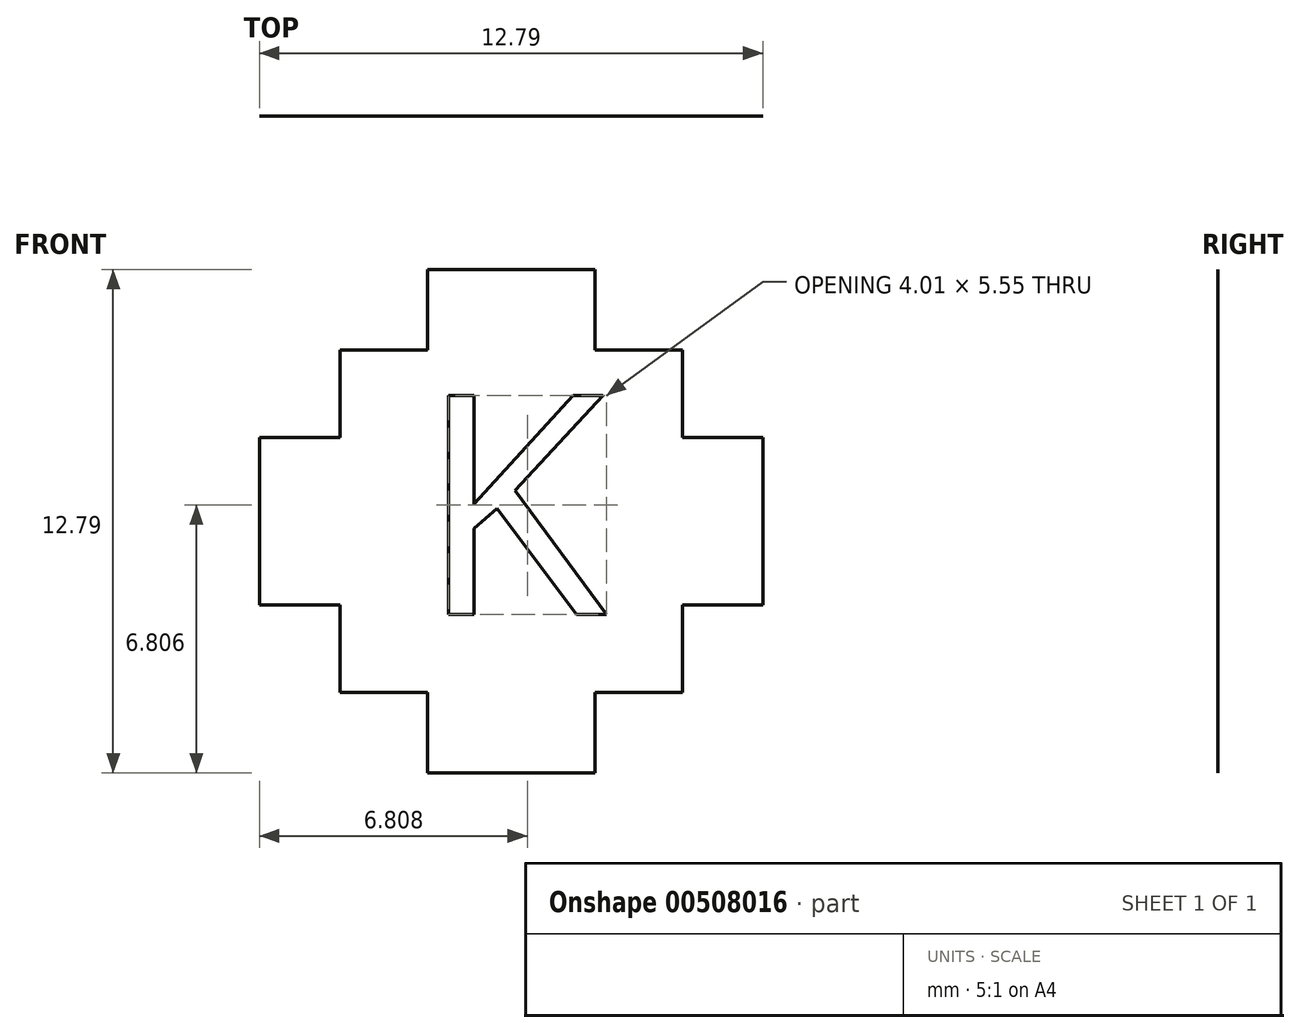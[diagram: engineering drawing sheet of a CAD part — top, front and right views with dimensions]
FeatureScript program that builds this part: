
annotation { "Feature Type Name" : "Feature", "Feature Type Description" : "" }
export const myFeature = defineFeature(function(context is Context, id is Id, definition is map)
    precondition{}
    {
        {
            var Q0;
            Q0=qCreatedBy(makeId("Front.planeOp"),FACE);
            var sketch = newSketch(context, id + "F0", { "sketchPlane" : qUnion([Q0])});
            skLineSegment(sketch, "E0", {"start": v(-17.35, 36.23) * mm, "end": v(-15.22, 36.23) * mm});
            skLineSegment(sketch, "E1", {"start": v(-15.22, 36.23) * mm, "end": v(-15.22, 34.18) * mm});
            skLineSegment(sketch, "E2", {"start": v(-15.22, 34.18) * mm, "end": v(-13, 34.18) * mm});
            skLineSegment(sketch, "E3", {"start": v(-13, 34.18) * mm, "end": v(-13, 31.96) * mm});
            skLineSegment(sketch, "E4", {"start": v(-13, 31.96) * mm, "end": v(-10.95, 31.96) * mm});
            skLineSegment(sketch, "E5", {"start": v(-10.95, 31.96) * mm, "end": v(-10.95, 29.83) * mm});
            skLineSegment(sketch, "E6", {"start": v(-17.35, 36.23) * mm, "end": v(-17.35, 28.94) * mm, "construction": true});
            skLineSegment(sketch, "E7.MirrorCS", {"start": v(-17.35, 36.23) * mm, "end": v(-19.48, 36.23) * mm});
            skLineSegment(sketch, "E8.MirrorCS", {"start": v(-19.48, 36.23) * mm, "end": v(-19.48, 34.18) * mm});
            skLineSegment(sketch, "E9.MirrorCS", {"start": v(-19.48, 34.18) * mm, "end": v(-21.7, 34.18) * mm});
            skLineSegment(sketch, "E10.MirrorCS", {"start": v(-21.7, 34.18) * mm, "end": v(-21.7, 31.96) * mm});
            skLineSegment(sketch, "E11.MirrorCS", {"start": v(-21.7, 31.96) * mm, "end": v(-23.74, 31.96) * mm});
            skLineSegment(sketch, "E12.MirrorCS", {"start": v(-23.74, 31.96) * mm, "end": v(-23.74, 29.83) * mm});
            skLineSegment(sketch, "E13", {"start": v(-23.74, 29.83) * mm, "end": v(-10.95, 29.83) * mm, "construction": true});
            skLineSegment(sketch, "E14.MirrorCS", {"start": v(-23.74, 27.7) * mm, "end": v(-23.74, 29.83) * mm});
            skLineSegment(sketch, "E15.MirrorCS", {"start": v(-21.7, 27.7) * mm, "end": v(-23.74, 27.7) * mm});
            skLineSegment(sketch, "E16.MirrorCS", {"start": v(-21.7, 25.48) * mm, "end": v(-21.7, 27.7) * mm});
            skLineSegment(sketch, "E17.MirrorCS", {"start": v(-19.48, 25.48) * mm, "end": v(-21.7, 25.48) * mm});
            skLineSegment(sketch, "E18.MirrorCS", {"start": v(-19.48, 23.44) * mm, "end": v(-19.48, 25.48) * mm});
            skLineSegment(sketch, "E19.MirrorCS", {"start": v(-17.35, 23.44) * mm, "end": v(-19.48, 23.44) * mm});
            skLineSegment(sketch, "E20.MirrorCS", {"start": v(-17.35, 23.44) * mm, "end": v(-15.22, 23.44) * mm});
            skLineSegment(sketch, "E21.MirrorCS", {"start": v(-15.22, 23.44) * mm, "end": v(-15.22, 25.48) * mm});
            skLineSegment(sketch, "E22.MirrorCS", {"start": v(-15.22, 25.48) * mm, "end": v(-13, 25.48) * mm});
            skLineSegment(sketch, "E23.MirrorCS", {"start": v(-13, 25.48) * mm, "end": v(-13, 27.7) * mm});
            skLineSegment(sketch, "E24.MirrorCS", {"start": v(-13, 27.7) * mm, "end": v(-10.95, 27.7) * mm});
            skLineSegment(sketch, "E25.MirrorCS", {"start": v(-10.95, 27.7) * mm, "end": v(-10.95, 29.83) * mm});
            skSolve(sketch);
        }
        {
            var Q0;
            Q0=makeQuery(id+"F0.imprint","IMPRINT",FACE,{"disambiguationData":[TD([[makeQuery(id+"F0.imprint","IMPRINT",EDGE,{"derivedFrom":sQuery(id+"F0.wireOp",EDGE,"E0")}),-1.0]])]});
            extrude(context, id + "F1", {"entities" : qUnion([Q0]), "depth" : .16 / 50.8 * mm, "offsetDistance" : 25 * mm});
        }
        {
            var Q0;
            Q0=makeQuery(id+"F1.opExtrude","CAP_FACE",FACE,{"disambiguationData":[OSD([sQuery(id+"F0.wireOp",EDGE,"E0"),sQuery(id+"F0.wireOp",EDGE,"E1"),sQuery(id+"F0.wireOp",EDGE,"E2"),sQuery(id+"F0.wireOp",EDGE,"E3"),sQuery(id+"F0.wireOp",EDGE,"E4"),sQuery(id+"F0.wireOp",EDGE,"E5"),sQuery(id+"F0.wireOp",EDGE,"E7.MirrorCS"),sQuery(id+"F0.wireOp",EDGE,"E8.MirrorCS"),sQuery(id+"F0.wireOp",EDGE,"E9.MirrorCS"),sQuery(id+"F0.wireOp",EDGE,"E10.MirrorCS"),sQuery(id+"F0.wireOp",EDGE,"E11.MirrorCS"),sQuery(id+"F0.wireOp",EDGE,"E12.MirrorCS"),sQuery(id+"F0.wireOp",EDGE,"E14.MirrorCS"),sQuery(id+"F0.wireOp",EDGE,"E15.MirrorCS"),sQuery(id+"F0.wireOp",EDGE,"E16.MirrorCS"),sQuery(id+"F0.wireOp",EDGE,"E17.MirrorCS"),sQuery(id+"F0.wireOp",EDGE,"E18.MirrorCS"),sQuery(id+"F0.wireOp",EDGE,"E19.MirrorCS"),sQuery(id+"F0.wireOp",EDGE,"E20.MirrorCS"),sQuery(id+"F0.wireOp",EDGE,"E21.MirrorCS"),sQuery(id+"F0.wireOp",EDGE,"E22.MirrorCS"),sQuery(id+"F0.wireOp",EDGE,"E23.MirrorCS"),sQuery(id+"F0.wireOp",EDGE,"E24.MirrorCS"),sQuery(id+"F0.wireOp",EDGE,"E25.MirrorCS")])],"isStart":false});
            var sketch = newSketch(context, id + "F2", { "sketchPlane" : qUnion([Q0])});
            skText(sketch, "E26", { "text": "K", "fontName": "OpenSans-Regular.ttf"});
            const initialGuessF2  = {"E26": [-0.0197, 0.02747, 1, 0, 0.0056]};
            skSetInitialGuess(sketch, initialGuessF2);
            skSolve(sketch);
        }
        {
            var Q0;
            Q0=makeQuery(id+"F2.imprint","IMPRINT",FACE,{"disambiguationData":[TD([[makeQuery(id+"F2.imprint","IMPRINT",EDGE,{"derivedFrom":sQuery(id+"F2.wireOp",EDGE,"E26.sketch_text.stroke-0")}),-1.0]])]});
            extrude(context, id + "F3", {"entities" : qUnion([Q0]), "operationType" : NewBodyOperationType.REMOVE, "oppositeDirection" : true, "depth" : 1 * mm, "offsetDistance" : 25 * mm});
        }
    });
